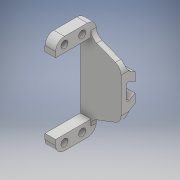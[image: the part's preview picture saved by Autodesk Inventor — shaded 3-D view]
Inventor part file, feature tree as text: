
AUTODESK INVENTOR PART (.ipt)
format: ipt  version: 2017 (Build 210142000, 142)  size: 223,744 bytes
history: native  units: mm
features: sketch x4, extrude x3, fillet x1, hole x1
ambient origin geometry x8: Origin, YZ Plane, XZ Plane, XY Plane, X Axis, Y Axis, Z Axis, Center Point
bodies: Solid1 (feature_tree)
feature tree (9):
  extrude  "Extrusion1"  Depth=20.0mm
  extrude  "Extrusion2"  Depth=23.0mm
  fillet  "Fillet1"  Radius=56.0mm
  hole  "Hole1"  [1 undecoded]
  extrude  "Extrusion3"  Depth=2.0mm
  sketch  "Sketch1"  dims[d0=40.0mm d1=20.0mm]
  sketch  "Sketch2"  dims[d2=8.0mm d3=23.0mm d5=56.0mm]
  sketch  "Sketch3"  dims[d6=23.0mm d7=5.5mm]
  sketch  "Sketch4"  dims[d8=5.5mm d9=4.9mm d10=2.7mm d11=2.7mm d13=5.0mm d14=5.0mm d15=17.5mm d16=17.5mm d17=5.0mm d18=5.0mm d19=5.0mm d20=5.0mm d21=23.0mm d22=0.0mm d23=6.0mm d24=23.0mm d25=11.5mm d26=0.0mm d27=0.0mm d28=5.0mm d29=5.0mm d30=4.0mm d31=10.0mm d32=5.0mm d33=4.0mm d34=10.0mm d35=4.0mm d36=6.0mm d37=5.0mm d38=2.0mm d39=90.0deg d40=15.0mm d41=0.0mm d42=56.0mm d43=23.0mm d44=0.0mm d45=1.0mm]
note: 1 required parameter value undecoded (feature->parameter linkage not recoverable at this tier; creation-order binding heuristic only, values carry confidence <= 0.55)
